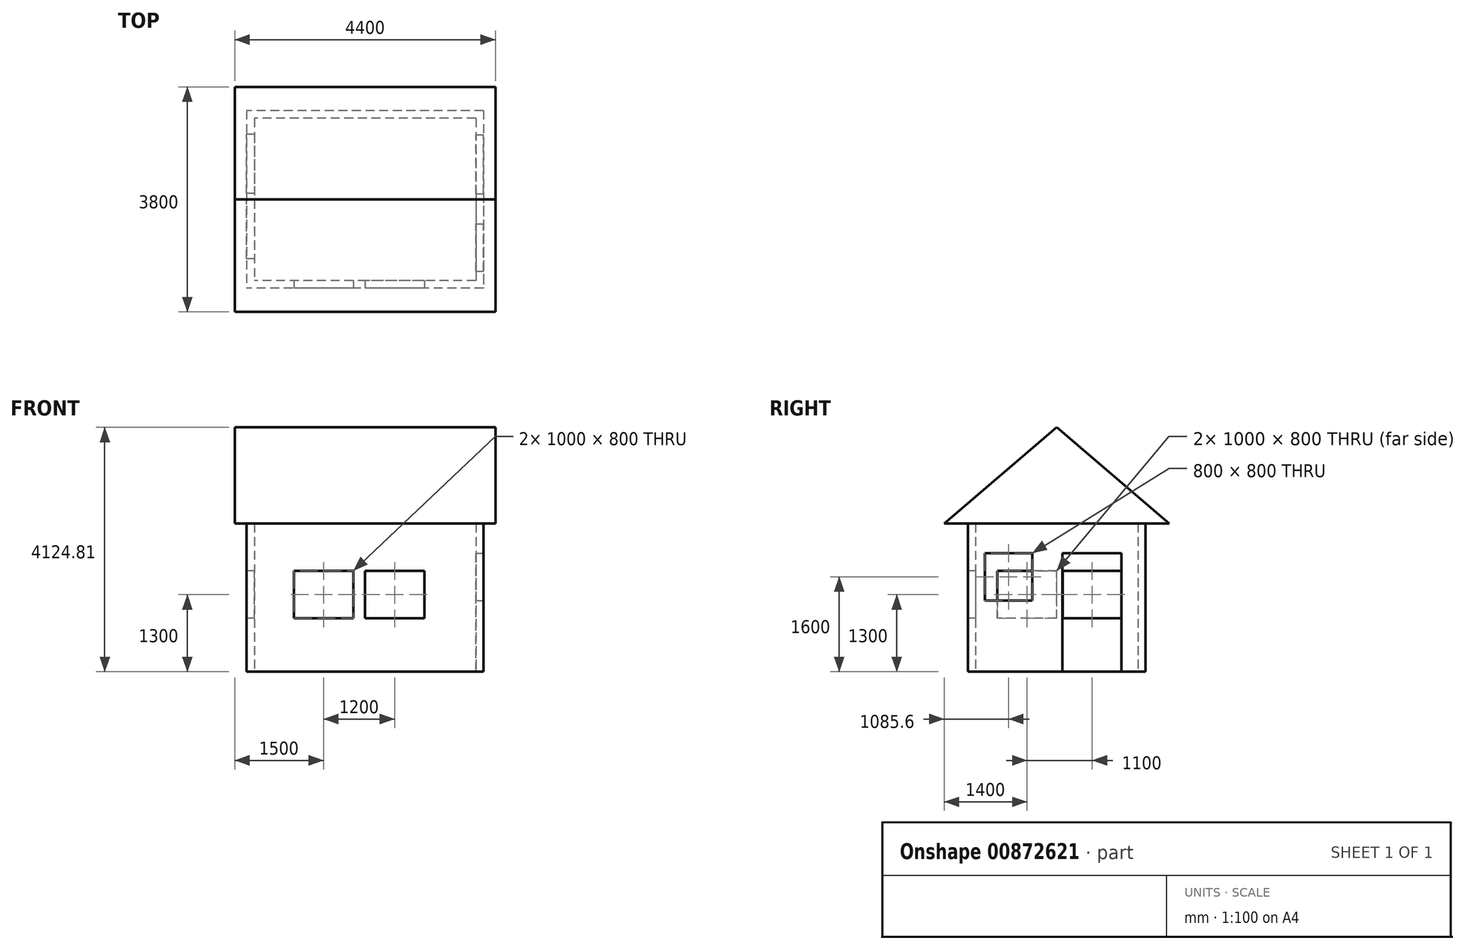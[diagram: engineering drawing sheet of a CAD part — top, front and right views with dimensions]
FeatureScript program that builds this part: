
annotation { "Feature Type Name" : "Feature", "Feature Type Description" : "" }
export const myFeature = defineFeature(function(context is Context, id is Id, definition is map)
    precondition{}
    {
        {
            var Q0;
            Q0=qCreatedBy(makeId("Top.planeOp"),FACE);
            var sketch = newSketch(context, id + "F0", { "sketchPlane" : qUnion([Q0])});
            skLineSegment(sketch, "E0.bottom", {"start": v(0, 0) * mm, "end": v(-4000, 0) * mm});
            skLineSegment(sketch, "E0.top", {"start": v(0, -3000) * mm, "end": v(-4000, -3000) * mm});
            skLineSegment(sketch, "E0.left", {"start": v(0, 0) * mm, "end": v(0, -3000) * mm});
            skLineSegment(sketch, "E0.right", {"start": v(-4000, 0) * mm, "end": v(-4000, -3000) * mm});
            skLineSegment(sketch, "E1.0", {"start": v(-130, -2870) * mm, "end": v(-3870, -2870) * mm});
            skLineSegment(sketch, "E1.1", {"start": v(-130, -130) * mm, "end": v(-130, -2870) * mm});
            skLineSegment(sketch, "E1.2", {"start": v(-130, -130) * mm, "end": v(-3870, -130) * mm});
            skLineSegment(sketch, "E1.3", {"start": v(-3870, -130) * mm, "end": v(-3870, -2870) * mm});
            skSolve(sketch);
        }
        {
            var Q0;
            Q0=makeQuery(id+"F0.imprint","IMPRINT",FACE,{"disambiguationData":[TD([[makeQuery(id+"F0.imprint","IMPRINT",EDGE,{"derivedFrom":sQuery(id+"F0.wireOp",EDGE,"E0.bottom")}),1.0]])]});
            extrude(context, id + "F1", {"entities" : qUnion([Q0]), "depth" : 2500 * mm, "offsetDistance" : 25 * mm});
        }
        {
            var Q0;
            Q0=makeQuery(id+"F1.opExtrude","SWEPT_FACE",FACE,{"disambiguationData":[OSD([sQuery(id+"F0.wireOp",EDGE,"E0.left")])]});
            var sketch = newSketch(context, id + "F2", { "sketchPlane" : qUnion([Q0])});
            skLineSegment(sketch, "E2.bottom", {"start": v(-1405.07, 0) * mm, "end": v(-405.07, 0) * mm});
            skLineSegment(sketch, "E2.top", {"start": v(-1405.07, 2000) * mm, "end": v(-405.07, 2000) * mm});
            skLineSegment(sketch, "E2.left", {"start": v(-1405.07, 0) * mm, "end": v(-1405.07, 2000) * mm});
            skLineSegment(sketch, "E2.right", {"start": v(-405.07, 0) * mm, "end": v(-405.07, 2000) * mm});
            skLineSegment(sketch, "E3.bottom", {"start": v(-2714.4, 2000) * mm, "end": v(-1914.4, 2000) * mm});
            skLineSegment(sketch, "E3.top", {"start": v(-2714.4, 1200) * mm, "end": v(-1914.4, 1200) * mm});
            skLineSegment(sketch, "E3.left", {"start": v(-2714.4, 2000) * mm, "end": v(-2714.4, 1200) * mm});
            skLineSegment(sketch, "E3.right", {"start": v(-1914.4, 2000) * mm, "end": v(-1914.4, 1200) * mm});
            skSolve(sketch);
        }
        {
            var Q0;
            Q0=makeQuery(id+"F2.imprint","IMPRINT",FACE,{"disambiguationData":[TD([[makeQuery(id+"F2.imprint","IMPRINT",EDGE,{"derivedFrom":sQuery(id+"F2.wireOp",EDGE,"E2.bottom")}),-1.0]])]});
            var Q1;
            Q1=makeQuery(id+"F2.imprint","IMPRINT",FACE,{"disambiguationData":[TD([[makeQuery(id+"F2.imprint","IMPRINT",EDGE,{"derivedFrom":sQuery(id+"F2.wireOp",EDGE,"E3.bottom")}),-1.0]])]});
            extrude(context, id + "F3", {"entities" : qUnion([Q0, Q1]), "operationType" : NewBodyOperationType.REMOVE, "oppositeDirection" : true, "depth" : 200 * mm, "offsetDistance" : 25 * mm});
        }
        {
            var Q0;
            Q0=makeQuery(id+"F1.opExtrude","SWEPT_FACE",FACE,{"disambiguationData":[OSD([sQuery(id+"F0.wireOp",EDGE,"E0.top")])]});
            var sketch = newSketch(context, id + "F4", { "sketchPlane" : qUnion([Q0])});
            skLineSegment(sketch, "E4.bottom", {"start": v(-1000, 1700) * mm, "end": v(-2000, 1700) * mm});
            skLineSegment(sketch, "E4.top", {"start": v(-1000, 900) * mm, "end": v(-2000, 900) * mm});
            skLineSegment(sketch, "E4.left", {"start": v(-1000, 1700) * mm, "end": v(-1000, 900) * mm});
            skLineSegment(sketch, "E4.right", {"start": v(-2000, 1700) * mm, "end": v(-2000, 900) * mm});
            skLineSegment(sketch, "E5.bottom", {"start": v(-2200, 1700) * mm, "end": v(-3200, 1700) * mm});
            skLineSegment(sketch, "E5.top", {"start": v(-2200, 900) * mm, "end": v(-3200, 900) * mm});
            skLineSegment(sketch, "E5.left", {"start": v(-2200, 1700) * mm, "end": v(-2200, 900) * mm});
            skLineSegment(sketch, "E5.right", {"start": v(-3200, 1700) * mm, "end": v(-3200, 900) * mm});
            skSolve(sketch);
        }
        {
            var Q0;
            Q0=makeQuery(id+"F4.imprint","IMPRINT",FACE,{"disambiguationData":[TD([[makeQuery(id+"F4.imprint","IMPRINT",EDGE,{"derivedFrom":sQuery(id+"F4.wireOp",EDGE,"E5.bottom")}),1.0]])]});
            var Q1;
            Q1=makeQuery(id+"F4.imprint","IMPRINT",FACE,{"disambiguationData":[TD([[makeQuery(id+"F4.imprint","IMPRINT",EDGE,{"derivedFrom":sQuery(id+"F4.wireOp",EDGE,"E4.bottom")}),1.0]])]});
            extrude(context, id + "F5", {"entities" : qUnion([Q0, Q1]), "operationType" : NewBodyOperationType.REMOVE, "oppositeDirection" : true, "depth" : 200 * mm, "offsetDistance" : 25 * mm});
        }
        {
            var Q0;
            Q0=makeQuery(id+"F1.opExtrude","SWEPT_FACE",FACE,{"disambiguationData":[OSD([sQuery(id+"F0.wireOp",EDGE,"E0.left")])]});
            var sketch = newSketch(context, id + "F6", { "sketchPlane" : qUnion([Q0])});
            skLineSegment(sketch, "E6.0", {"start": v(0, 2500) * mm, "end": v(-3000, 2500) * mm});
            skLineSegment(sketch, "E7", {"start": v(-3400, 2500) * mm, "end": v(-1500, 4124.8) * mm});
            skLineSegment(sketch, "E8", {"start": v(-1500, 4124.8) * mm, "end": v(400, 2500) * mm});
            skLineSegment(sketch, "E9", {"start": v(400, 2500) * mm, "end": v(0, 2500) * mm});
            skLineSegment(sketch, "E10", {"start": v(-3000, 2500) * mm, "end": v(-3400, 2500) * mm});
            skSolve(sketch);
        }
        {
            var Q0;
            Q0=makeQuery(id+"F6.imprint","IMPRINT",FACE,{"disambiguationData":[TD([[makeQuery(id+"F6.imprint","IMPRINT",EDGE,{"derivedFrom":sQuery(id+"F6.wireOp",EDGE,"E6.0")}),-1.0]])]});
            extrude(context, id + "F7", {"entities" : qUnion([Q0]), "operationType" : NewBodyOperationType.ADD, "depth" : 200 * mm, "offsetDistance" : 25 * mm, "hasSecondDirection" : true, "secondDirectionOppositeDirection" : true, "secondDirectionDepth" : 4200 * mm});
        }
        {
            var Q0;
            Q0=makeQuery(id+"F1.opExtrude","SWEPT_FACE",FACE,{"disambiguationData":[OSD([sQuery(id+"F0.wireOp",EDGE,"E0.right")])]});
            var sketch = newSketch(context, id + "F8", { "sketchPlane" : qUnion([Q0])});
            skLineSegment(sketch, "E11.bottom", {"start": v(2500, 1700) * mm, "end": v(1500, 1700) * mm});
            skLineSegment(sketch, "E11.top", {"start": v(2500, 900) * mm, "end": v(1500, 900) * mm});
            skLineSegment(sketch, "E11.left", {"start": v(2500, 1700) * mm, "end": v(2500, 900) * mm});
            skLineSegment(sketch, "E11.right", {"start": v(1500, 1700) * mm, "end": v(1500, 900) * mm});
            skPoint(sketch, "E12.oppositeSnap0", {"position": v(2000, 900) * mm});
            skLineSegment(sketch, "E12.bottom", {"start": v(1400, 1700) * mm, "end": v(400, 1700) * mm});
            skLineSegment(sketch, "E12.top", {"start": v(1400, 900) * mm, "end": v(400, 900) * mm});
            skLineSegment(sketch, "E12.left", {"start": v(1400, 1700) * mm, "end": v(1400, 900) * mm});
            skLineSegment(sketch, "E12.right", {"start": v(400, 1700) * mm, "end": v(400, 900) * mm});
            skSolve(sketch);
        }
        {
            var Q0;
            Q0=makeQuery(id+"F8.imprint","IMPRINT",FACE,{"disambiguationData":[TD([[makeQuery(id+"F8.imprint","IMPRINT",EDGE,{"derivedFrom":sQuery(id+"F8.wireOp",EDGE,"E12.bottom")}),1.0]])]});
            var Q1;
            Q1=makeQuery(id+"F8.imprint","IMPRINT",FACE,{"disambiguationData":[TD([[makeQuery(id+"F8.imprint","IMPRINT",EDGE,{"derivedFrom":sQuery(id+"F8.wireOp",EDGE,"E11.bottom")}),1.0]])]});
            extrude(context, id + "F9", {"entities" : qUnion([Q0, Q1]), "operationType" : NewBodyOperationType.REMOVE, "oppositeDirection" : true, "depth" : 200 * mm, "offsetDistance" : 25 * mm});
        }
    });
